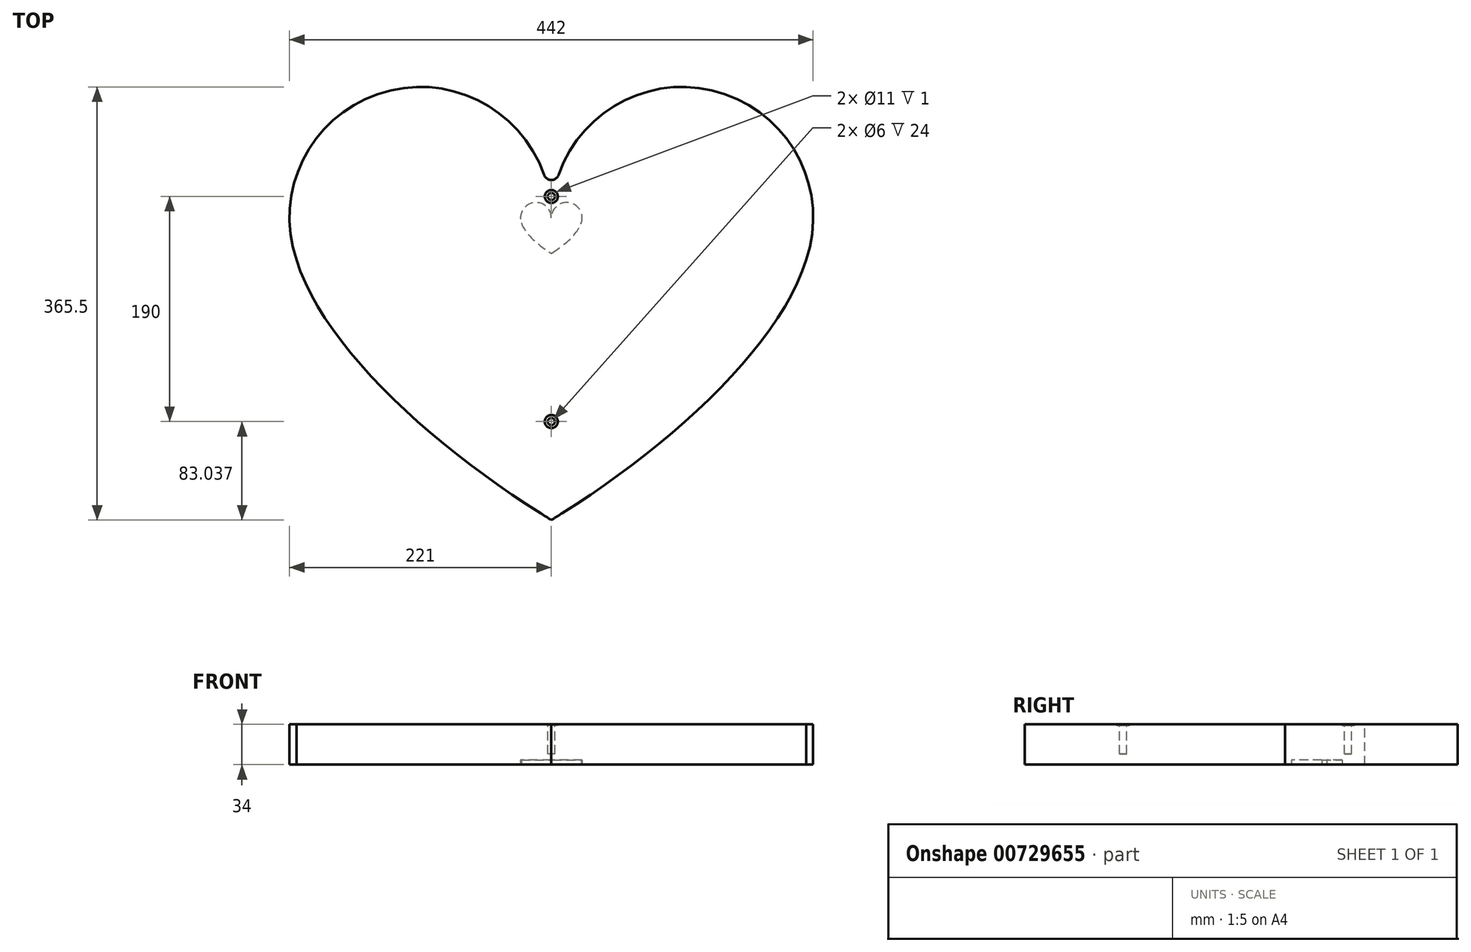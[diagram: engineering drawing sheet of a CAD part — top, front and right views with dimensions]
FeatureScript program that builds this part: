
annotation { "Feature Type Name" : "Feature", "Feature Type Description" : "" }
export const myFeature = defineFeature(function(context is Context, id is Id, definition is map)
    precondition{}
    {
        {
            var Q0;
            Q0=qCreatedBy(makeId("Top.planeOp"),FACE);
            var sketch = newSketch(context, id + "F0", { "sketchPlane" : qUnion([Q0])});
            skLineSegment(sketch, "E0", {"start": v(0, 0) * mm, "end": v(13, 0) * mm});
            skLineSegment(sketch, "E1", {"start": v(0, 0) * mm, "end": v(-13, 0) * mm});
            skCircle(sketch, "E2", {"center": v(13, 0) * mm, "radius": 13 * mm});
            skCircle(sketch, "E3", {"center": v(-13, 0) * mm, "radius": 13 * mm});
            skLineSegment(sketch, "E4", {"start": v(0, 0) * mm, "end": v(0, -30) * mm});
            skPoint(sketch, "E5.visualSharp", {"position": v(0, -30) * mm});
            skLineSegment(sketch, "E6", {"start": v(-13, 0) * mm, "end": v(-13, 5) * mm});
            skLineSegment(sketch, "E7", {"start": v(13, 0) * mm, "end": v(13, 5) * mm});
            skLineSegment(sketch, "E8", {"start": v(-26, 0) * mm, "end": v(-26, -10) * mm});
            skLineSegment(sketch, "E9", {"start": v(26, 0) * mm, "end": v(26, -10) * mm});
            skFitSpline(sketch, "E10", {"points": [v(-26, 0) * mm, v(0, -30) * mm], "startDerivative": vector(0, -30) * mm, "endDerivative": vector(39, -24) * mm});
            skFitSpline(sketch, "E11", {"points": [v(0, -30) * mm, v(26, 0) * mm], "startDerivative": vector(39, 24) * mm, "endDerivative": vector(0, 30) * mm});
            skLineSegment(sketch, "E12", {"start": v(0, -30) * mm, "end": v(0, -22) * mm});
            skArc(sketch, "E13.filletArc", {"start": v(-1.07, -29.33) * mm, "mid": v(0, -29.64) * mm, "end": v(1.07, -29.33) * mm});
            skSolve(sketch);
        }
        {
            var Q0;
            Q0=qSketchRegion(id+"F0",true);
            extrude(context, id + "F1", {"entities" : qUnion([Q0]), "depth" : 4 * mm, "offsetDistance" : 25 * mm});
        }
        {
            var Q0;
            Q0=makeQuery(id+"F1.opExtrude","SWEPT_BODY",BODY,{"disambiguationData":[OSD([sQuery(id+"F0.wireOp",EDGE,"E2"),sQuery(id+"F0.wireOp",EDGE,"E3"),sQuery(id+"F0.wireOp",EDGE,"E10"),sQuery(id+"F0.wireOp",EDGE,"E11"),sQuery(id+"F0.wireOp",EDGE,"E13.filletArc")])]});
            var Q1;
            Q1=sQuery(id+"F0.wireOp",VERTEX,"E4.start");
            transform(context, id + "F2", {"entities" : qUnion([Q0]), "transformType" : TransformType.SCALE_UNIFORMLY, "scale" : 8.5, "scalePoint" : qUnion([Q1]), "makeCopy" : true});
        }
        {
            var Q0;
            Q0=makeQuery(id+"F2.opPattern","COPY",EDGE,{"derivedFrom":makeQuery(id+"F1.opExtrude","SWEPT_EDGE",EDGE,{"disambiguationData":[OSD([sQuery(id+"F0.wireOp",EDGE,"E2"),sQuery(id+"F0.wireOp",EDGE,"E3"),sQuery(id+"F0.wireOp",EDGE,"E4")])]}),"instanceName":"1"});
            fillet(context, id + "F3", {"entities" : qUnion([Q0]), "radius" : 6.5 * mm, "tangentPropagation" : true, "allowEdgeOverflow" : false});
        }
        {
            var Q0;
            Q0=makeQuery(id+"F2.opPattern","COPY",FACE,{"derivedFrom":makeQuery(id+"F1.opExtrude","CAP_FACE",FACE,{"disambiguationData":[OSD([sQuery(id+"F0.wireOp",EDGE,"E2"),sQuery(id+"F0.wireOp",EDGE,"E3"),sQuery(id+"F0.wireOp",EDGE,"E10"),sQuery(id+"F0.wireOp",EDGE,"E11"),sQuery(id+"F0.wireOp",EDGE,"E13.filletArc")])],"isStart":false}),"instanceName":"1"});
            var sketch = newSketch(context, id + "F4", { "sketchPlane" : qUnion([Q0])});
            skCircle(sketch, "E14", {"center": v(0, 18.04) * mm, "radius": 5.5 * mm});
            skCircle(sketch, "E15", {"center": v(0, -171.96) * mm, "radius": 5.5 * mm});
            skSolve(sketch);
        }
        {
            var Q0;
            Q0 = qSketchRegion(id + "F4", true);
            extrude(context, id + "F5", {"entities" : qUnion([Q0]), "operationType" : NewBodyOperationType.REMOVE, "oppositeDirection" : true, "depth" : 1 * mm, "offsetDistance" : 25 * mm});
        }
        {
            var Q0;
            Q0 = qSketchRegion(id + "F4", true);
            extrude(context, id + "F6", {"entities" : qUnion([Q0]), "operationType" : NewBodyOperationType.REMOVE, "oppositeDirection" : true, "depth" : 0.5 * mm, "offsetDistance" : 25 * mm});
        }
        {
            var Q0;
            Q0=makeQuery(id+"F2.opPattern","COPY",FACE,{"derivedFrom":makeQuery(id+"F1.opExtrude","CAP_FACE",FACE,{"disambiguationData":[OSD([sQuery(id+"F0.wireOp",EDGE,"E2"),sQuery(id+"F0.wireOp",EDGE,"E3"),sQuery(id+"F0.wireOp",EDGE,"E10"),sQuery(id+"F0.wireOp",EDGE,"E11"),sQuery(id+"F0.wireOp",EDGE,"E13.filletArc")])],"isStart":false}),"instanceName":"1"});
            var sketch = newSketch(context, id + "F7", { "sketchPlane" : qUnion([Q0])});
            skCircle(sketch, "E16", {"center": v(0, 18.04) * mm, "radius": 3 * mm});
            skCircle(sketch, "E17", {"center": v(0, -171.96) * mm, "radius": 3 * mm});
            skSolve(sketch);
        }
        {
            var Q0;
            Q0 = qSketchRegion(id + "F7", true);
            extrude(context, id + "F8", {"entities" : qUnion([Q0]), "operationType" : NewBodyOperationType.REMOVE, "oppositeDirection" : true, "depth" : 25 * mm, "offsetDistance" : 25 * mm});
        }
    });
